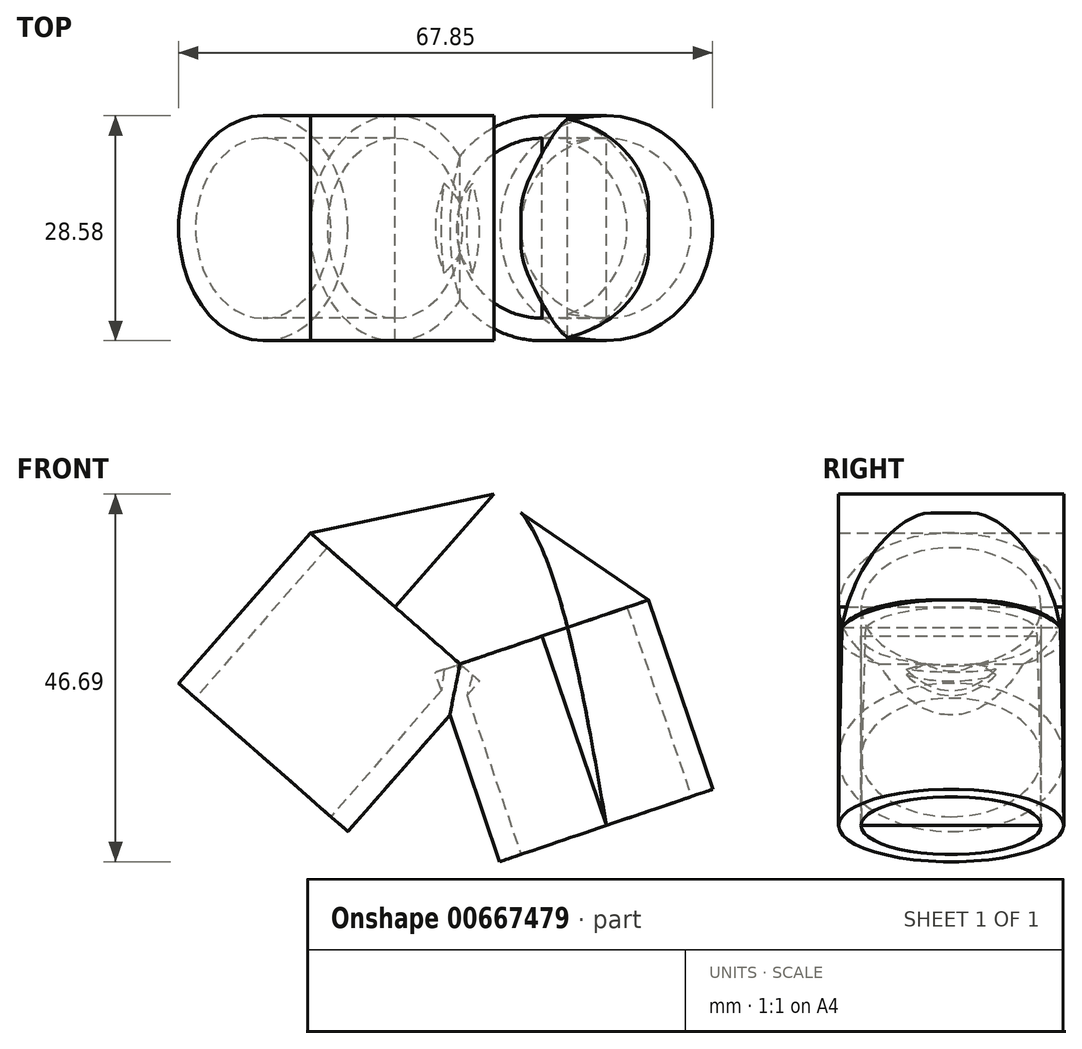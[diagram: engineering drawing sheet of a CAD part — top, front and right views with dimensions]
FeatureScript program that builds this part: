
annotation { "Feature Type Name" : "Feature", "Feature Type Description" : "" }
export const myFeature = defineFeature(function(context is Context, id is Id, definition is map)
    precondition{}
    {
        {
            var Q0;
            Q0=qCreatedBy(makeId("Front.planeOp"),FACE);
            var sketch = newSketch(context, id + "F0", { "sketchPlane" : qUnion([Q0])});
            skLineSegment(sketch, "E0", {"start": v(0, 0) * mm, "end": v(29.3, 33.43) * mm});
            skLineSegment(sketch, "E1", {"start": v(29.3, 33.43) * mm, "end": v(43.6, -8.65) * mm});
            skFitSpline(sketch, "E2", {"points": [v(0, 0) * mm, v(29.3, 33.43) * mm, v(43.6, -8.65) * mm], "startDerivative": vector(66.08, 104.63) * mm, "endDerivative": vector(21.12, -121.93) * mm});
            skLineSegment(sketch, "E3", {"start": v(43.6, -8.65) * mm, "end": v(28.62, -13.74) * mm});
            skLineSegment(sketch, "E4", {"start": v(16.74, 19.1) * mm, "end": v(29.3, 33.43) * mm});
            skLineSegment(sketch, "E5", {"start": v(0, 0) * mm, "end": v(16.74, 19.1) * mm});
            skLineSegment(sketch, "E6", {"start": v(43.6, -8.65) * mm, "end": v(35.42, 15.4) * mm});
            skLineSegment(sketch, "E7", {"start": v(0, 0) * mm, "end": v(8.12, -7.11) * mm});
            skLineSegment(sketch, "E8", {"start": v(35.42, 15.4) * mm, "end": v(25, 11.85) * mm});
            skLineSegment(sketch, "E9", {"start": v(25, 11.85) * mm, "end": v(16.74, 19.1) * mm});
            skLineSegment(sketch, "E10", {"start": v(16.74, 19.1) * mm, "end": v(6, 28.52) * mm});
            skLineSegment(sketch, "E11", {"start": v(6, 28.52) * mm, "end": v(29.3, 33.43) * mm});
            skLineSegment(sketch, "E12", {"start": v(35.42, 15.4) * mm, "end": v(48.95, 20) * mm});
            skLineSegment(sketch, "E13", {"start": v(48.95, 20) * mm, "end": v(29.3, 33.43) * mm});
            skLineSegment(sketch, "E14", {"start": v(0, 0) * mm, "end": v(43.6, -8.65) * mm});
            skLineSegment(sketch, "E15", {"start": v(21.8, -4.33) * mm, "end": v(29.3, 33.43) * mm});
            skSolve(sketch);
        }
        {
            var Q0;
            Q0=sQuery(id+"F0.wireOp",EDGE,"E3");
            cPlane(context, id + "F1", {"entities" : qUnion([Q0]), "cplaneType" : CPlaneType.LINE_ANGLE, "offset" : 0 * mm, "angle" : 90 * degree, "width" : 152.4 * mm, "height" : 152.4 * mm});
        }
        {
            var Q0;
            Q0=qCreatedBy(id+"F1.planeOp",FACE);
            var sketch = newSketch(context, id + "F2", { "sketchPlane" : qUnion([Q0])});
            skCircle(sketch, "E16", {"center": v(38.47, 0) * mm, "radius": 11.43 * mm});
            skCircle(sketch, "E17", {"center": v(38.47, 0) * mm, "radius": 14.29 * mm});
            skSolve(sketch);
        }
        {
            var Q0;
            Q0=makeQuery(id+"F2.imprint","IMPRINT",FACE,{"disambiguationData":[TD([[makeQuery(id+"F2.imprint","IMPRINT",EDGE,{"derivedFrom":sQuery(id+"F2.wireOp",EDGE,"E16")}),-1.0]])]});
            var Q1;
            Q1=sQuery(id+"F0.wireOp",EDGE,"E6");
            sweep(context, id + "F3", {"profiles" : qUnion([Q0]), "path" : qUnion([Q1])});
        }
        {
            var Q0;
            Q0=sQuery(id+"F0.wireOp",EDGE,"E7");
            cPlane(context, id + "F4", {"entities" : qUnion([Q0]), "cplaneType" : CPlaneType.LINE_ANGLE, "offset" : 25.4 * mm, "angle" : 90 * degree, "width" : 152.4 * mm, "height" : 152.4 * mm});
        }
        {
            var Q0;
            Q0=qCreatedBy(id+"F4.planeOp",FACE);
            var sketch = newSketch(context, id + "F5", { "sketchPlane" : qUnion([Q0])});
            skCircle(sketch, "E18", {"center": v(0, 0) * mm, "radius": 11.43 * mm});
            skCircle(sketch, "E19", {"center": v(0, 0) * mm, "radius": 14.29 * mm});
            skSolve(sketch);
        }
        {
            var Q0;
            Q0=makeQuery(id+"F5.imprint","IMPRINT",FACE,{"disambiguationData":[TD([[makeQuery(id+"F5.imprint","IMPRINT",EDGE,{"derivedFrom":sQuery(id+"F5.wireOp",EDGE,"E18")}),-1.0]])]});
            var Q1;
            Q1=sQuery(id+"F0.wireOp",EDGE,"E5");
            sweep(context, id + "F6", {"operationType" : NewBodyOperationType.ADD, "profiles" : qUnion([Q0]), "path" : qUnion([Q1])});
        }
        {
            var Q0;
            {var subQ0=sQuery(id+"F0.wireOp",EDGE,"E13");var subQ1=sQuery(id+"F0.wireOp",EDGE,"E2");var subQ2=makeQuery(id+"F0.imprint","INTERSECT",VERTEX,{"derivedFrom":[subQ1,subQ0]});Q0=makeQuery(id+"F0.imprint","IMPRINT",FACE,{"disambiguationData":[TD([[makeQuery(id+"F0.imprint","IMPRINT",EDGE,{"disambiguationData":[TD([[subQ2,-1.0]])],"derivedFrom":subQ1}),1.0]])]});}
            var Q1;
            {var subQ5=sQuery(id+"F0.wireOp",EDGE,"E4");Q1=makeQuery(id+"F0.imprint","IMPRINT",FACE,{"disambiguationData":[TD([[makeQuery(id+"F0.imprint","IMPRINT",EDGE,{"derivedFrom":subQ5}),1.0]])]});}
            var Q2;
            {var subQ0=sQuery(id+"F0.wireOp",EDGE,"E10");var subQ1=sQuery(id+"F0.wireOp",EDGE,"E2");var subQ2=makeQuery(id+"F0.imprint","INTERSECT",VERTEX,{"derivedFrom":[subQ1,subQ0]});Q2=makeQuery(id+"F0.imprint","IMPRINT",FACE,{"disambiguationData":[TD([[makeQuery(id+"F0.imprint","IMPRINT",EDGE,{"disambiguationData":[TD([[subQ2,-1.0]])],"derivedFrom":subQ1}),1.0]])]});}
            var Q3;
            {var subQ0=sQuery(id+"F0.wireOp",EDGE,"E1");Q3=makeQuery(id+"F0.imprint","IMPRINT",FACE,{"disambiguationData":[TD([[makeQuery(id+"F0.imprint","IMPRINT",EDGE,{"derivedFrom":subQ0}),-1.0]])]});}
            var Q4;
            {var subQ0=sQuery(id+"F0.wireOp",EDGE,"E4");Q4=makeQuery(id+"F0.imprint","IMPRINT",FACE,{"disambiguationData":[TD([[makeQuery(id+"F0.imprint","IMPRINT",EDGE,{"derivedFrom":subQ0}),-1.0]])]});}
            var Q5;
            {var subQ0=sQuery(id+"F0.wireOp",EDGE,"E1");Q5=makeQuery(id+"F0.imprint","IMPRINT",FACE,{"disambiguationData":[TD([[makeQuery(id+"F0.imprint","IMPRINT",EDGE,{"derivedFrom":subQ0}),1.0]])]});}
            extrude(context, id + "F7", {"entities" : qUnion([Q0, Q1, Q2, Q3, Q4, Q5]), "operationType" : NewBodyOperationType.ADD, "depth" : 14.29 * mm, "offsetDistance" : 25.4 * mm, "hasSecondDirection" : true, "secondDirectionOppositeDirection" : true, "secondDirectionDepth" : 14.29 * mm});
        }
        {
            var Q0;
            Q0=makeQuery(id+"F7.opExtrude","CAP_EDGE",EDGE,{"disambiguationData":[OSD([sQuery(id+"F0.wireOp",EDGE,"E13")])],"isStart":true});
            var Q1;
            Q1=makeQuery(id+"F7.opExtrude","CAP_EDGE",EDGE,{"disambiguationData":[OSD([sQuery(id+"F0.wireOp",EDGE,"E11")])],"isStart":true});
            var Q2;
            Q2=makeQuery(id+"F7.opExtrude","SWEPT_EDGE",EDGE,{"disambiguationData":[OSD([sQuery(id+"F0.wireOp",EDGE,"E1"),sQuery(id+"F0.wireOp",EDGE,"E2"),sQuery(id+"F0.wireOp",EDGE,"E4"),sQuery(id+"F0.wireOp",EDGE,"76aQiBmm-nc9Y-1zkB-9hD7-2VkLzmBfmQF2"),sQuery(id+"F0.wireOp",EDGE,"E11"),sQuery(id+"F0.wireOp",EDGE,"E13")])]});
            var Q3;
            Q3=makeQuery(id+"F7.opExtrude","CAP_EDGE",EDGE,{"disambiguationData":[OSD([sQuery(id+"F0.wireOp",EDGE,"E11")])],"isStart":false});
            var Q4;
            Q4=makeQuery(id+"F7.opExtrude","CAP_EDGE",EDGE,{"disambiguationData":[OSD([sQuery(id+"F0.wireOp",EDGE,"E13")])],"isStart":false});
            fillet(context, id + "F8", {"entities" : qUnion([Q0, Q1, Q2, Q3, Q4]), "radius" : 11.75 * mm, "tangentPropagation" : true, "allowEdgeOverflow" : false});
        }
    });
